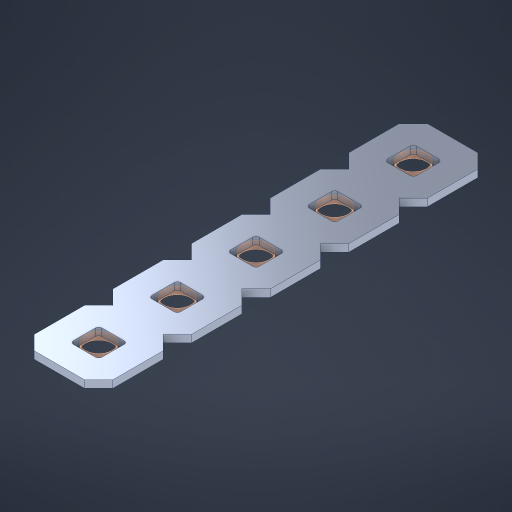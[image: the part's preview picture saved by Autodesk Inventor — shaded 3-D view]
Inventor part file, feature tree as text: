
AUTODESK INVENTOR PART (.ipt)
format: ipt  version: 2023 (Build 270158000, 158)  size: 324,608 bytes
history: native  units: in
note: dims shown in document units (in); Inventor stores cm internally (conversion verified against a paired STEP export)
features: other x6, extrude x4, sketch x2, pattern_linear x1
ambient origin geometry x8: Origin, YZ Plane, XZ Plane, XY Plane, X Axis, Y Axis, Z Axis, Center Point
bodies: Solid1 (feature_tree), Body (feature_tree)
feature tree (13):
  pattern_linear  "Rectangular Pattern1"  Spacing1=0.09in  [1 undecoded]
  sketch  "Sketch1"  dims[d1=0.5in]
  sketch  "Sketch2"  dims[d2=0.182in d3=0.09in d4=0.09in d5=0.09in d6=0.09in d7=0.09in d8=0.09in d9=0.09in d10=0.09in d11=0.02in d13=0.0in d14=0.172in d15=0.0625in d16=0.0in d19=0.5in d22=0.5in]
  other  "Srf1"
  other  "Srf126"
  other  "Srf127"
  other  "Srf128"
  other  "Srf129"
  other  "Circle"
  extrude  "ExtrusionSrf126"  Depth=0.09in
  extrude  "ExtrusionSrf127"  Depth=0.09in
  extrude  "ExtrusionSrf128"  Depth=0.09in
  extrude  "ExtrusionSrf129"  Depth=0.09in
note: 1 required parameter value undecoded (feature->parameter linkage not recoverable at this tier; creation-order binding heuristic only, values carry confidence <= 0.55)
